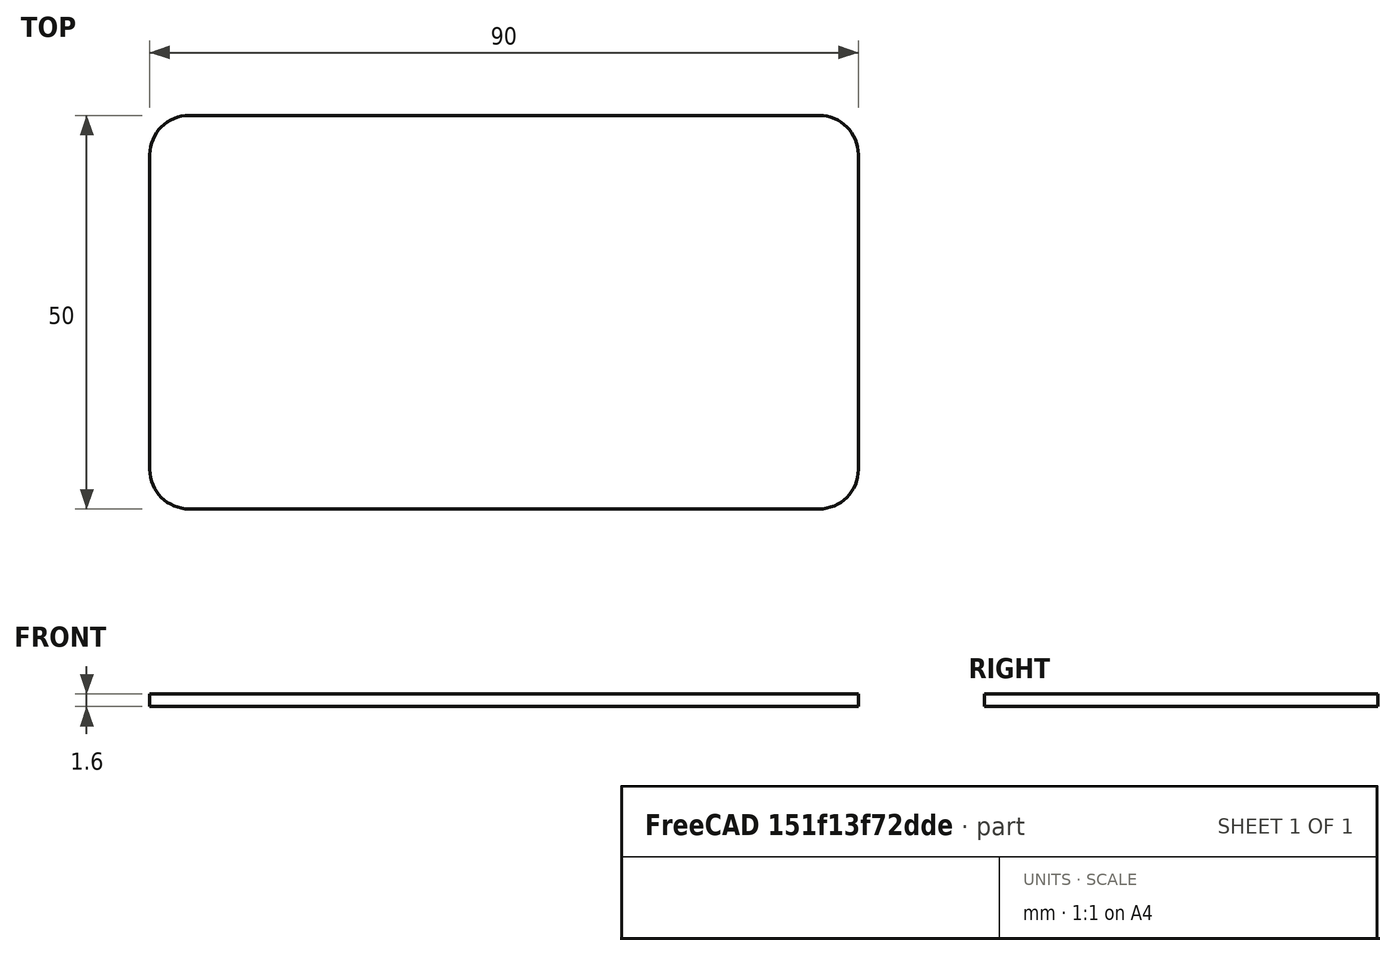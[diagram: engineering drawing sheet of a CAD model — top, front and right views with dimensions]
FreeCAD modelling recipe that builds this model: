
FCSTD DOCUMENT  (FreeCAD 0.20R29177 +426 (Git))
Label: LISN_BOX
License: All rights reserved
LicenseURL: http://en.wikipedia.org/wiki/All_rights_reserved
objects: Sketcher::SketchObject×2, PartDesign::Pad×1, PartDesign::Body×1, App::Part×1
note: 5 computed .brp shape members not serialized (recipe doc carries the construction recipe); baked Part::Feature solids carry a one-line shape summary decoded from their .brp

FEATURE [Sketcher::SketchObject] Sketch
  FullyConstrained = true
  MapMode = 5
  Support = -> [XY_Plane001]
  sketch-geometry (8):
    g0: LineSegment StartX=-40 StartY=25 StartZ=0 EndX=40 EndY=25 EndZ=0
    g1: LineSegment StartX=45 StartY=20 StartZ=0 EndX=45 EndY=-20 EndZ=0
    g2: LineSegment StartX=40 StartY=-25 StartZ=0 EndX=-40 EndY=-25 EndZ=0
    g3: LineSegment StartX=-45 StartY=-20 StartZ=0 EndX=-45 EndY=20 EndZ=0
    g4: ArcOfCircle CenterX=-40 CenterY=20 CenterZ=0 NormalX=0 NormalY=0 NormalZ=1 AngleXU=0 Radius=5 StartAngle=1.5708 EndAngle=3.14159
    g5: ArcOfCircle CenterX=40 CenterY=20 CenterZ=0 NormalX=0 NormalY=0 NormalZ=1 AngleXU=0 Radius=5 StartAngle=0 EndAngle=1.5708
    g6: ArcOfCircle CenterX=40 CenterY=-20 CenterZ=0 NormalX=0 NormalY=0 NormalZ=1 AngleXU=0 Radius=5 StartAngle=4.71239 EndAngle=6.28319
    g7: ArcOfCircle CenterX=-40 CenterY=-20 CenterZ=0 NormalX=0 NormalY=0 NormalZ=1 AngleXU=0 Radius=5 StartAngle=3.14159 EndAngle=4.71239
  constraints (19):
    c: Horizontal(g0)
    c: Horizontal(g2)
    c: Vertical(g1)
    c: Vertical(g3)
    c: Tangent(g0,g4) = 1.5708
    c: Tangent(g3,g4) = 1.5708
    c: Tangent(g0,g5) = 1.5708
    c: Tangent(g1,g5) = 1.5708
    c: Tangent(g1,g6) = 1.5708
    c: Tangent(g2,g6) = 1.5708
    c: Tangent(g3,g7) = 1.5708
    c: Tangent(g2,g7) = 1.5708
    c: Equal(g4,g5)
    c: Equal(g5,g6)
    c: Equal(g6,g7)
    c: Radius(g4) = 5
    c: DistanceY(g2,g0) = 50
    c: DistanceX(g3,g1) = 90
    c: Symmetric(g4,g6,g-1)
FEATURE [PartDesign::Pad] Pad  label="FR4"
  Direction = (0,0,1)
  Length = 1.6
  Length2 = 10
  Profile = -> Sketch
  ReferenceAxis = -> Sketch [N_Axis]
  Type = 0
FEATURE [Sketcher::SketchObject] Sketch001  label="pad"
  FullyConstrained = true
  MapMode = 5
  Support = -> [XY_Plane001]
  sketch-geometry (20):
    g0: LineSegment StartX=-45 StartY=11 StartZ=0 EndX=-39 EndY=11 EndZ=0
    g1: LineSegment StartX=-39 StartY=11 StartZ=0 EndX=-39 EndY=5 EndZ=0
    g2: LineSegment StartX=-39 StartY=5 StartZ=0 EndX=-45 EndY=5 EndZ=0
    g3: LineSegment StartX=-45 StartY=5 StartZ=0 EndX=-45 EndY=11 EndZ=0
    g4: LineSegment StartX=-45 StartY=-5 StartZ=0 EndX=-39 EndY=-5 EndZ=0
    g5: LineSegment StartX=-39 StartY=-5 StartZ=0 EndX=-39 EndY=-11 EndZ=0
    g6: LineSegment StartX=-39 StartY=-11 StartZ=0 EndX=-45 EndY=-11 EndZ=0
    g7: LineSegment StartX=-45 StartY=-11 StartZ=0 EndX=-45 EndY=-5 EndZ=0
    g8: LineSegment StartX=39 StartY=-5 StartZ=0 EndX=45 EndY=-5 EndZ=0
    g9: LineSegment StartX=45 StartY=-5 StartZ=0 EndX=45 EndY=-11 EndZ=0
    g10: LineSegment StartX=45 StartY=-11 StartZ=0 EndX=39 EndY=-11 EndZ=0
    g11: LineSegment StartX=39 StartY=-11 StartZ=0 EndX=39 EndY=-5 EndZ=0
    g12: LineSegment StartX=39 StartY=11 StartZ=0 EndX=45 EndY=11 EndZ=0
    g13: LineSegment StartX=45 StartY=11 StartZ=0 EndX=45 EndY=5 EndZ=0
    g14: LineSegment StartX=45 StartY=5 StartZ=0 EndX=39 EndY=5 EndZ=0
    g15: LineSegment StartX=39 StartY=5 StartZ=0 EndX=39 EndY=11 EndZ=0
    g16: LineSegment StartX=-45 StartY=25 StartZ=0 EndX=45 EndY=25 EndZ=0
    g17: LineSegment StartX=45 StartY=25 StartZ=0 EndX=45 EndY=-25 EndZ=0
    g18: LineSegment StartX=45 StartY=-25 StartZ=0 EndX=-45 EndY=-25 EndZ=0
    g19: LineSegment StartX=-45 StartY=-25 StartZ=0 EndX=-45 EndY=25 EndZ=0
  constraints (57):
    c: Coincident(g0,g1)
    c: Coincident(g1,g2)
    c: Coincident(g2,g3)
    c: Coincident(g3,g0)
    c: Horizontal(g0)
    c: Horizontal(g2)
    c: Vertical(g1)
    c: Vertical(g3)
    c: Coincident(g4,g5)
    c: Coincident(g5,g6)
    c: Coincident(g6,g7)
    c: Coincident(g7,g4)
    c: Horizontal(g4)
    c: Horizontal(g6)
    c: Vertical(g5)
    c: Vertical(g7)
    c: Coincident(g8,g9)
    c: Coincident(g9,g10)
    c: Coincident(g10,g11)
    c: Coincident(g11,g8)
    c: Horizontal(g8)
    c: Horizontal(g10)
    c: Vertical(g9)
    c: Vertical(g11)
    c: Coincident(g12,g13)
    c: Coincident(g13,g14)
    c: Coincident(g14,g15)
    c: Coincident(g15,g12)
    c: Horizontal(g12)
    c: Horizontal(g14)
    c: Vertical(g13)
    c: Vertical(g15)
    c: Equal(g2,g1)
    c: Equal(g4,g5)
    c: Equal(g5,g11)
    c: Equal(g11,g8)
    c: Equal(g8,g14)
    c: Equal(g14,g15)
    c: Equal(g15,g2)
    c: DistanceY(g3,g3) = 6
    c: Symmetric(g4,g2,g-1)
    c: Symmetric(g4,g8,g-2)
    c: DistanceX(g6,g9) = 90
    c: Horizontal(g0,g12)
    c: Vertical(g13,g8)
    c: DistanceY(g4,g2) = 10
    c: Coincident(g16,g17)
    c: Coincident(g17,g18)
    c: Coincident(g18,g19)
    c: Coincident(g19,g16)
    c: Horizontal(g16)
    c: Horizontal(g18)
    c: Vertical(g17)
    c: Vertical(g19)
    c: DistanceX(g16,g16) = 90
    c: DistanceY(g17,g17) = 50
    c: Symmetric(g16,g18,g-1)
FEATURE [PartDesign::Body] Body  label="PCB_part"
  Group = -> [Sketch,Pad,Sketch001]
  Origin = -> Origin001
  Tip = -> Pad
FEATURE [App::Part] Part  label="PCB"
  Group = -> [Body]
  Origin = -> Origin
